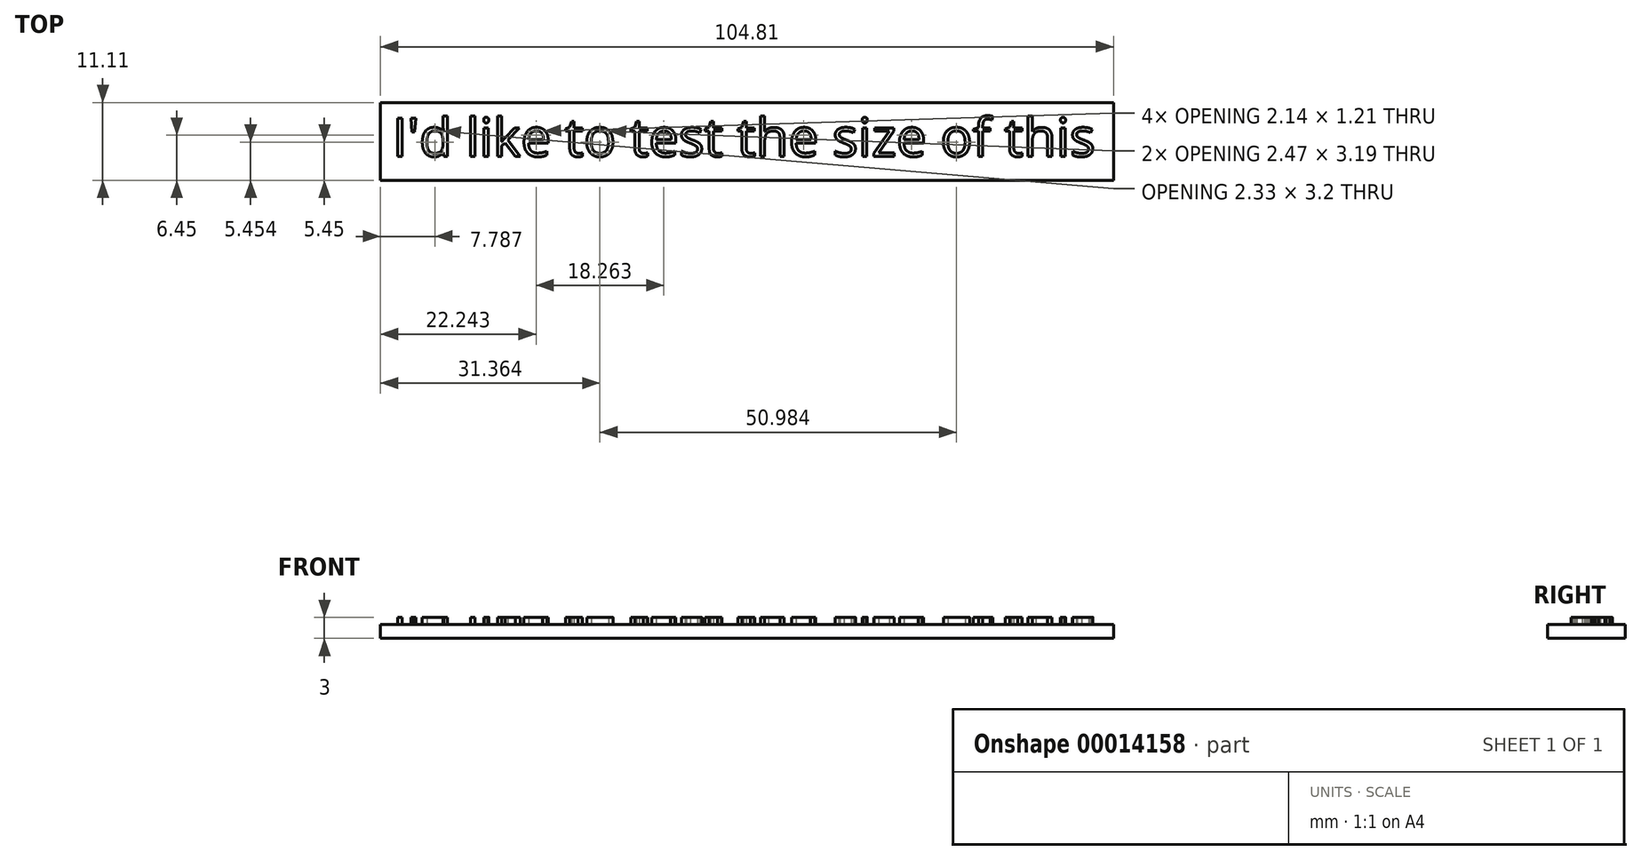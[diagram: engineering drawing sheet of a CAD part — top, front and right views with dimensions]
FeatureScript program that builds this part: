
annotation { "Feature Type Name" : "Feature", "Feature Type Description" : "" }
export const myFeature = defineFeature(function(context is Context, id is Id, definition is map)
    precondition{}
    {
        {
            var Q0;
            Q0=qCreatedBy(makeId("Top.planeOp"),FACE);
            var sketch = newSketch(context, id + "F0", { "sketchPlane" : qUnion([Q0])});
            skText(sketch, "E0", { "text": "I\'d like to test the size of this", "fontName": "OpenSans-Regular.ttf"});
            const initialGuessF0  = {"E0": [0, 0, 1, 0, 0.0055]};
            skSetInitialGuess(sketch, initialGuessF0);
            skSolve(sketch);
        }
        {
            var Q0;
            Q0 = qSketchRegion(id + "F0", true);
            extrude(context, id + "F1", {"entities" : qUnion([Q0]), "depth" : 1 * mm});
        }
        {
            var Q0;
            Q0=qCreatedBy(makeId("Top.planeOp"),FACE);
            var sketch = newSketch(context, id + "F2", { "sketchPlane" : qUnion([Q0])});
            skLineSegment(sketch, "E1.bottom", {"start": v(-1.73, -3.41) * mm, "end": v(103.08, -3.41) * mm});
            skLineSegment(sketch, "E1.top", {"start": v(-1.73, 7.7) * mm, "end": v(103.08, 7.7) * mm});
            skLineSegment(sketch, "E1.left", {"start": v(-1.73, -3.41) * mm, "end": v(-1.73, 7.7) * mm});
            skLineSegment(sketch, "E1.right", {"start": v(103.08, -3.41) * mm, "end": v(103.08, 7.7) * mm});
            skSolve(sketch);
        }
        {
            var Q0;
            Q0=makeQuery(id+"F2.imprint","IMPRINT",FACE,{"disambiguationData":[TD([[makeQuery(id+"F2.imprint","IMPRINT",EDGE,{"derivedFrom":sQuery(id+"F2.wireOp",EDGE,"E1.bottom")}),1.0]])]});
            extrude(context, id + "F3", {"entities" : qUnion([Q0]), "oppositeDirection" : true, "depth" : 2 * mm});
        }
    });
